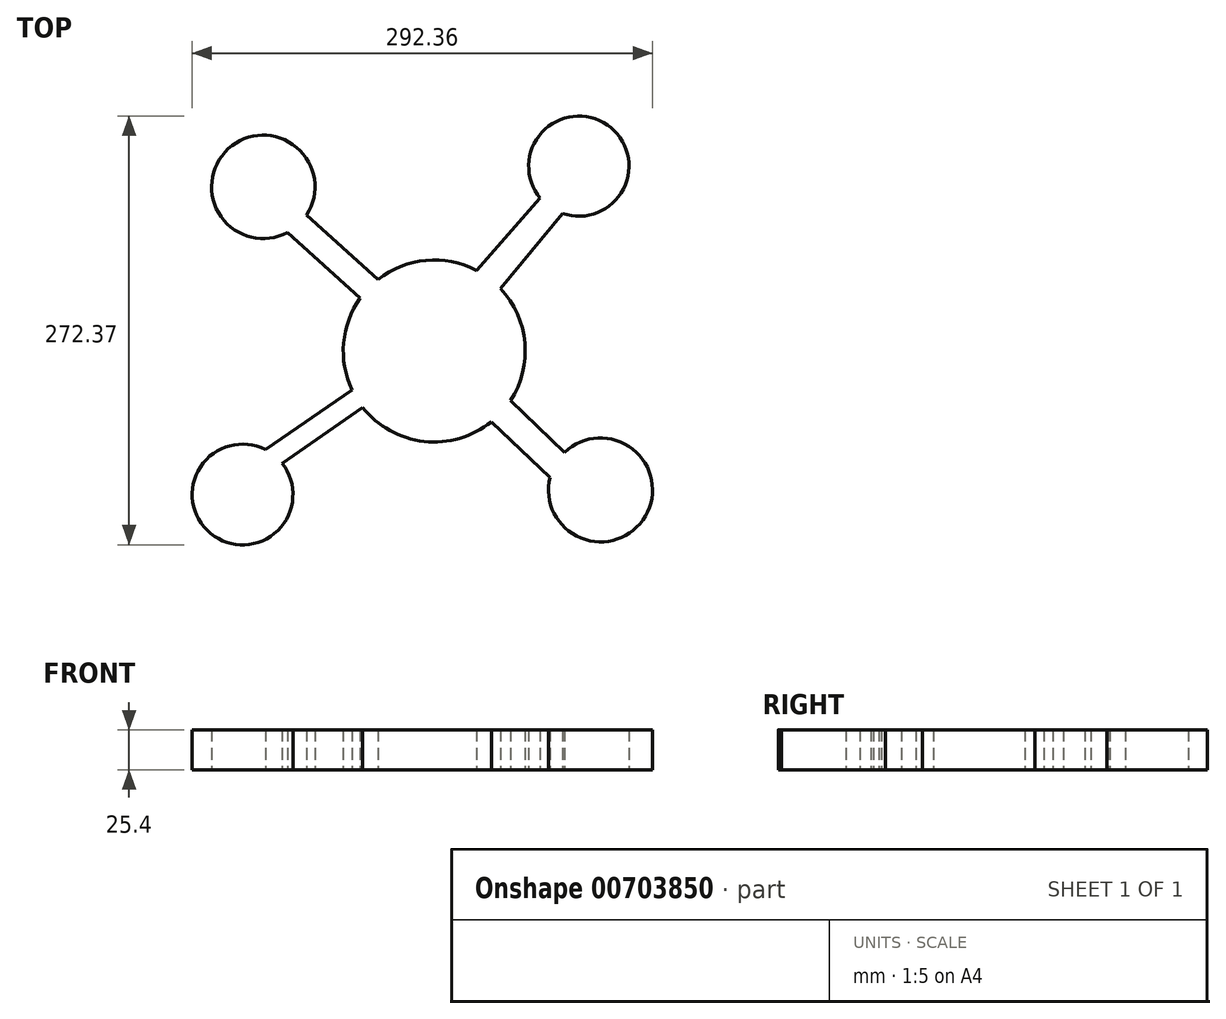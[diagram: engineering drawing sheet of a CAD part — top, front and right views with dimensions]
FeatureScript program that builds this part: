
annotation { "Feature Type Name" : "Feature", "Feature Type Description" : "" }
export const myFeature = defineFeature(function(context is Context, id is Id, definition is map)
    precondition{}
    {
        {
            var Q0;
            Q0=qCreatedBy(makeId("Top.planeOp"),FACE);
            var sketch = newSketch(context, id + "F0", { "sketchPlane" : qUnion([Q0])});
            skCircle(sketch, "E0", {"center": v(0, 0) * mm, "radius": 57.79 * mm});
            skLineSegment(sketch, "E1", {"start": v(-47.07, 33.51) * mm, "end": v(-94.6, 76.58) * mm});
            skLineSegment(sketch, "E2", {"start": v(-35.73, 45.41) * mm, "end": v(-81.03, 86.45) * mm});
            skLineSegment(sketch, "E3", {"start": v(36.27, -44.99) * mm, "end": v(82.06, -88.22) * mm});
            skLineSegment(sketch, "E4", {"start": v(48.4, -31.57) * mm, "end": v(91.18, -72.24) * mm});
            skCircle(sketch, "E5", {"center": v(91.82, 117.41) * mm, "radius": 31.82 * mm});
            skCircle(sketch, "E6", {"center": v(-108.6, 104.26) * mm, "radius": 32.82 * mm});
            skCircle(sketch, "E7", {"center": v(-121.75, -91.15) * mm, "radius": 32 * mm});
            skCircle(sketch, "E8", {"center": v(105.6, -88.22) * mm, "radius": 33.01 * mm});
            skLineSegment(sketch, "E9", {"start": v(-107.1, -62.7) * mm, "end": v(-52.25, -24.68) * mm});
            skLineSegment(sketch, "E10", {"start": v(-96.65, -71.3) * mm, "end": v(-45.38, -35.77) * mm});
            skLineSegment(sketch, "E11", {"start": v(67.34, 97.09) * mm, "end": v(26.83, 51.18) * mm});
            skLineSegment(sketch, "E12", {"start": v(81.4, 87.35) * mm, "end": v(42.06, 39.63) * mm});
            skSolve(sketch);
        }
        {
            var Q0;
            Q0 = qSketchRegion(id + "F0", true);
            extrude(context, id + "F1", {"entities" : qUnion([Q0]), "depth" : 25.4 * mm, "offsetDistance" : 25.4 * mm});
        }
    });
